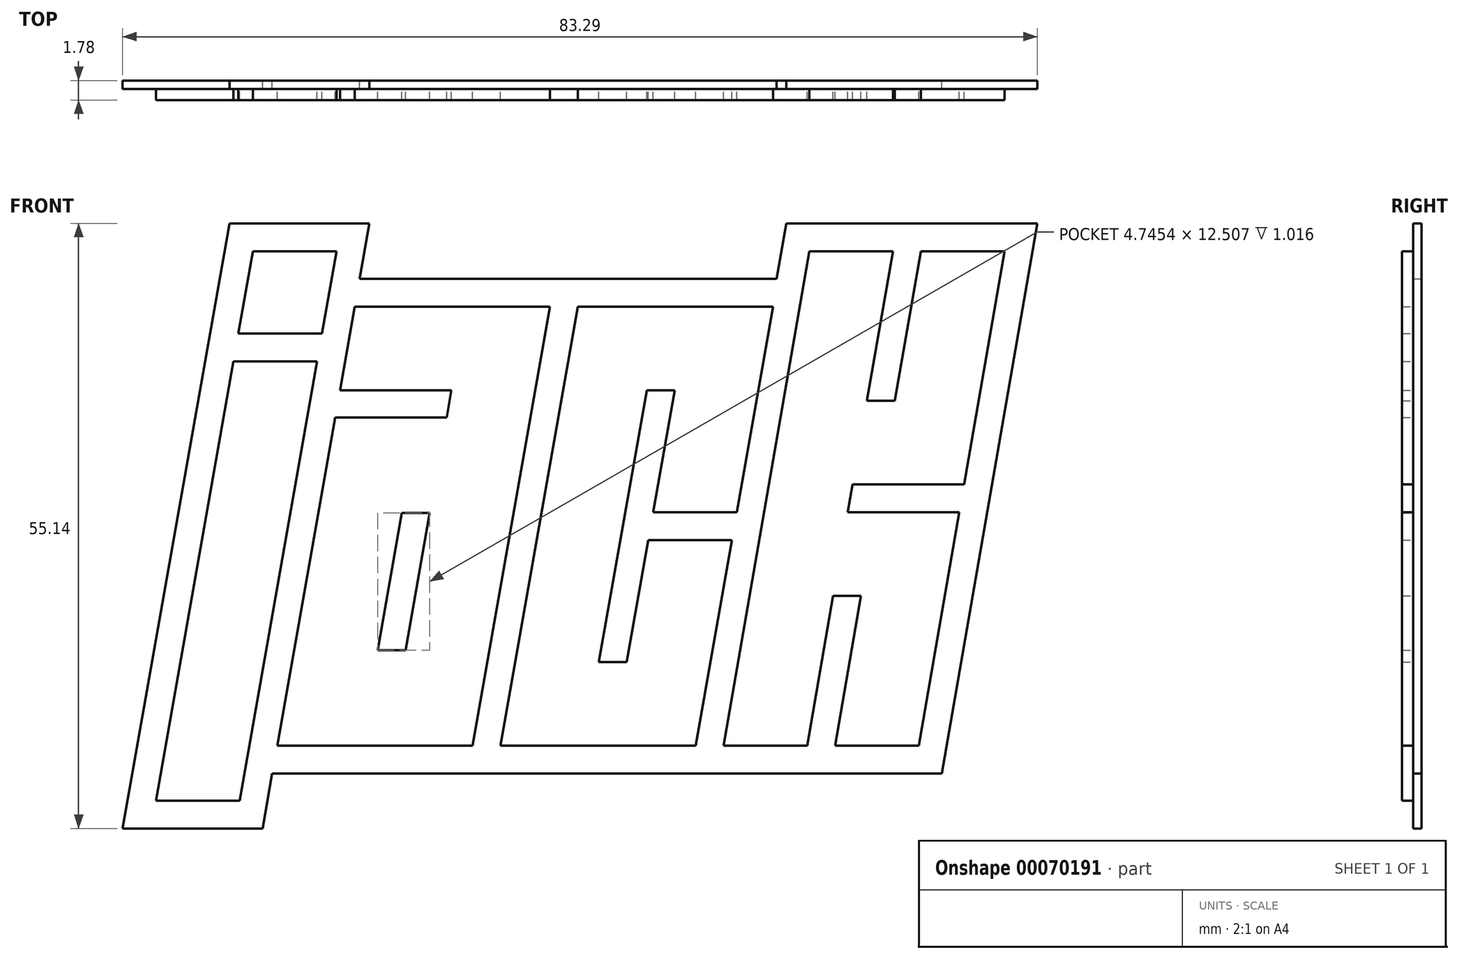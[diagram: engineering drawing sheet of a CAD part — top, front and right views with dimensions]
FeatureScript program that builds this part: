
annotation { "Feature Type Name" : "Feature", "Feature Type Description" : "" }
export const myFeature = defineFeature(function(context is Context, id is Id, definition is map)
    precondition{}
    {
        {
            var Q0;
            Q0=qCreatedBy(makeId("Front.planeOp"),FACE);
            var sketch = newSketch(context, id + "F0", { "sketchPlane" : qUnion([Q0])});
            skLineSegment(sketch, "E0", {"start": v(0, 0) * mm, "end": v(6.17, 35.02) * mm});
            skLineSegment(sketch, "E1", {"start": v(6.17, 35.02) * mm, "end": v(13.8, 35.02) * mm});
            skLineSegment(sketch, "E2", {"start": v(13.8, 35.02) * mm, "end": v(7.62, 0) * mm});
            skLineSegment(sketch, "E3", {"start": v(0, 0) * mm, "end": v(7.62, 0) * mm});
            skLineSegment(sketch, "E4", {"start": v(6.62, 37.56) * mm, "end": v(14.24, 37.56) * mm});
            skLineSegment(sketch, "E5", {"start": v(14.24, 37.56) * mm, "end": v(15.57, 45.06) * mm});
            skLineSegment(sketch, "E6", {"start": v(15.57, 45.06) * mm, "end": v(7.95, 45.06) * mm});
            skLineSegment(sketch, "E7", {"start": v(7.95, 45.06) * mm, "end": v(6.62, 37.56) * mm});
            skLineSegment(sketch, "E8", {"start": v(0, 0) * mm, "end": v(-0.88, -5) * mm});
            skLineSegment(sketch, "E9", {"start": v(-0.88, -5) * mm, "end": v(6.74, -5) * mm});
            skLineSegment(sketch, "E10", {"start": v(6.74, -5) * mm, "end": v(7.62, 0) * mm});
            skLineSegment(sketch, "E11.0", {"start": v(-3.9, -7.54) * mm, "end": v(8.83, -7.54) * mm});
            skLineSegment(sketch, "E11.1", {"start": v(-2.5, 0.44) * mm, "end": v(-3.9, -7.54) * mm});
            skLineSegment(sketch, "E11.2", {"start": v(18.55, 47.6) * mm, "end": v(5.81, 47.6) * mm});
            skLineSegment(sketch, "E11.5", {"start": v(-2.5, 0.44) * mm, "end": v(5.81, 47.6) * mm});
            skLineSegment(sketch, "E12", {"start": v(10.16, 0) * mm, "end": v(27.94, 0) * mm});
            skLineSegment(sketch, "E13", {"start": v(27.94, 0) * mm, "end": v(35, 40.02) * mm});
            skLineSegment(sketch, "E14", {"start": v(35, 40.02) * mm, "end": v(17.22, 40.02) * mm});
            skLineSegment(sketch, "E15", {"start": v(17.22, 40.02) * mm, "end": v(15.87, 32.4) * mm});
            skLineSegment(sketch, "E16", {"start": v(15.87, 32.4) * mm, "end": v(26.03, 32.4) * mm});
            skLineSegment(sketch, "E17", {"start": v(26.03, 32.4) * mm, "end": v(25.6, 29.9) * mm});
            skLineSegment(sketch, "E18", {"start": v(25.6, 29.9) * mm, "end": v(15.43, 29.9) * mm});
            skLineSegment(sketch, "E19", {"start": v(21.52, 21.2) * mm, "end": v(19.31, 8.7) * mm});
            skLineSegment(sketch, "E20", {"start": v(19.31, 8.7) * mm, "end": v(21.85, 8.7) * mm});
            skLineSegment(sketch, "E21", {"start": v(21.85, 8.7) * mm, "end": v(24.06, 21.2) * mm});
            skLineSegment(sketch, "E22", {"start": v(24.06, 21.2) * mm, "end": v(21.52, 21.2) * mm});
            skLineSegment(sketch, "E23", {"start": v(15.43, 29.9) * mm, "end": v(12.9, 29.9) * mm});
            skLineSegment(sketch, "E24", {"start": v(15.57, 45.06) * mm, "end": v(15.57, 47.6) * mm, "construction": true});
            skLineSegment(sketch, "E25", {"start": v(6.62, 37.56) * mm, "end": v(6.62, 35.02) * mm, "construction": true});
            skLineSegment(sketch, "E26", {"start": v(10.16, 0) * mm, "end": v(15.43, 29.9) * mm});
            skLineSegment(sketch, "E27", {"start": v(19.31, 8.7) * mm, "end": v(11.7, 8.7) * mm, "construction": true});
            skLineSegment(sketch, "E28", {"start": v(21.85, 8.7) * mm, "end": v(29.47, 8.7) * mm, "construction": true});
            skLineSegment(sketch, "E29", {"start": v(8.83, -7.54) * mm, "end": v(9.71, -2.54) * mm});
            skLineSegment(sketch, "E30", {"start": v(9.71, -2.54) * mm, "end": v(70.68, -2.54) * mm});
            skLineSegment(sketch, "E31", {"start": v(24.06, 21.2) * mm, "end": v(24.06, 29.9) * mm, "construction": true});
            skLineSegment(sketch, "E32", {"start": v(21.85, 8.7) * mm, "end": v(21.85, 0) * mm, "construction": true});
            skLineSegment(sketch, "E33", {"start": v(30.48, 0) * mm, "end": v(37.54, 40.02) * mm});
            skLineSegment(sketch, "E34", {"start": v(37.54, 40.02) * mm, "end": v(55.32, 40.02) * mm});
            skLineSegment(sketch, "E35", {"start": v(55.32, 40.02) * mm, "end": v(52.01, 21.28) * mm});
            skLineSegment(sketch, "E36", {"start": v(52.01, 21.28) * mm, "end": v(44.4, 21.28) * mm});
            skLineSegment(sketch, "E37", {"start": v(44.4, 21.28) * mm, "end": v(46.35, 32.4) * mm});
            skLineSegment(sketch, "E38", {"start": v(46.35, 32.4) * mm, "end": v(43.81, 32.4) * mm});
            skLineSegment(sketch, "E39", {"start": v(43.81, 32.4) * mm, "end": v(39.44, 7.62) * mm});
            skLineSegment(sketch, "E40", {"start": v(39.44, 7.62) * mm, "end": v(41.98, 7.62) * mm});
            skLineSegment(sketch, "E41", {"start": v(41.98, 7.62) * mm, "end": v(43.94, 18.74) * mm});
            skLineSegment(sketch, "E42", {"start": v(43.94, 18.74) * mm, "end": v(51.56, 18.74) * mm});
            skLineSegment(sketch, "E43", {"start": v(51.56, 18.74) * mm, "end": v(48.26, 0) * mm});
            skLineSegment(sketch, "E44", {"start": v(48.26, 0) * mm, "end": v(30.48, 0) * mm});
            skLineSegment(sketch, "E45", {"start": v(31.06, 17.72) * mm, "end": v(33.6, 17.72) * mm, "construction": true});
            skLineSegment(sketch, "E46", {"start": v(27.94, 0) * mm, "end": v(27.94, -2.54) * mm, "construction": true});
            skLineSegment(sketch, "E47", {"start": v(44.4, 21.28) * mm, "end": v(44.4, 18.74) * mm, "construction": true});
            skLineSegment(sketch, "E48", {"start": v(44.4, 21.28) * mm, "end": v(41.85, 21.28) * mm, "construction": true});
            skLineSegment(sketch, "E49", {"start": v(43.81, 32.4) * mm, "end": v(43.81, 40.02) * mm, "construction": true});
            skLineSegment(sketch, "E50", {"start": v(39.44, 7.62) * mm, "end": v(39.44, 0) * mm, "construction": true});
            skLineSegment(sketch, "E51", {"start": v(39.44, 7.62) * mm, "end": v(31.82, 7.62) * mm, "construction": true});
            skLineSegment(sketch, "E52", {"start": v(46.35, 32.4) * mm, "end": v(53.97, 32.4) * mm, "construction": true});
            skLineSegment(sketch, "E53", {"start": v(41.98, 7.62) * mm, "end": v(49.6, 7.62) * mm, "construction": true});
            skLineSegment(sketch, "E54", {"start": v(58.62, 45.06) * mm, "end": v(50.8, 0) * mm});
            skLineSegment(sketch, "E55", {"start": v(50.8, 0) * mm, "end": v(58.42, 0) * mm});
            skLineSegment(sketch, "E56", {"start": v(58.42, 0) * mm, "end": v(60.79, 13.64) * mm});
            skLineSegment(sketch, "E57", {"start": v(60.79, 13.64) * mm, "end": v(63.33, 13.64) * mm});
            skLineSegment(sketch, "E58", {"start": v(63.33, 13.64) * mm, "end": v(60.96, 0) * mm});
            skLineSegment(sketch, "E59", {"start": v(60.96, 0) * mm, "end": v(68.58, 0) * mm});
            skLineSegment(sketch, "E60", {"start": v(68.58, 0) * mm, "end": v(72.27, 21.26) * mm});
            skLineSegment(sketch, "E61", {"start": v(72.27, 21.26) * mm, "end": v(62.1, 21.26) * mm});
            skLineSegment(sketch, "E62", {"start": v(62.1, 21.26) * mm, "end": v(62.55, 23.8) * mm});
            skLineSegment(sketch, "E63", {"start": v(62.55, 23.8) * mm, "end": v(72.7, 23.8) * mm});
            skLineSegment(sketch, "E64", {"start": v(72.7, 23.8) * mm, "end": v(76.4, 45.06) * mm});
            skLineSegment(sketch, "E65", {"start": v(76.4, 45.06) * mm, "end": v(68.78, 45.06) * mm});
            skLineSegment(sketch, "E66", {"start": v(68.78, 45.06) * mm, "end": v(66.41, 31.42) * mm});
            skLineSegment(sketch, "E67", {"start": v(66.41, 31.42) * mm, "end": v(63.87, 31.42) * mm});
            skLineSegment(sketch, "E68", {"start": v(63.87, 31.42) * mm, "end": v(66.24, 45.06) * mm});
            skLineSegment(sketch, "E69", {"start": v(66.24, 45.06) * mm, "end": v(58.62, 45.06) * mm});
            skLineSegment(sketch, "E70", {"start": v(48.26, 0) * mm, "end": v(50.8, 0) * mm, "construction": true});
            skLineSegment(sketch, "E71", {"start": v(56.25, 31.42) * mm, "end": v(63.87, 31.42) * mm, "construction": true});
            skLineSegment(sketch, "E72", {"start": v(63.87, 31.42) * mm, "end": v(63.87, 23.8) * mm, "construction": true});
            skLineSegment(sketch, "E73", {"start": v(63.33, 13.64) * mm, "end": v(63.33, 21.26) * mm, "construction": true});
            skLineSegment(sketch, "E74", {"start": v(66.41, 31.42) * mm, "end": v(74.03, 31.42) * mm, "construction": true});
            skLineSegment(sketch, "E75", {"start": v(63.33, 13.64) * mm, "end": v(70.95, 13.64) * mm, "construction": true});
            skLineSegment(sketch, "E76", {"start": v(60.79, 13.64) * mm, "end": v(53.17, 13.64) * mm, "construction": true});
            skLineSegment(sketch, "E77", {"start": v(72.27, 21.26) * mm, "end": v(72.27, 23.8) * mm, "construction": true});
            skLineSegment(sketch, "E78", {"start": v(57.98, -2.54) * mm, "end": v(60.52, -2.54) * mm, "construction": true});
            skLineSegment(sketch, "E79", {"start": v(68.78, 45.06) * mm, "end": v(68.78, 23.8) * mm, "construction": true});
            skLineSegment(sketch, "E80", {"start": v(68.58, 0) * mm, "end": v(68.58, 21.26) * mm, "construction": true});
            skLineSegment(sketch, "E81", {"start": v(18.55, 47.6) * mm, "end": v(17.66, 42.56) * mm});
            skLineSegment(sketch, "E82", {"start": v(17.66, 42.56) * mm, "end": v(55.64, 42.56) * mm});
            skLineSegment(sketch, "E83", {"start": v(55.64, 42.56) * mm, "end": v(56.52, 47.6) * mm});
            skLineSegment(sketch, "E84", {"start": v(79.38, 47.6) * mm, "end": v(70.68, -2.54) * mm});
            skLineSegment(sketch, "E85", {"start": v(56.52, 47.6) * mm, "end": v(79.38, 47.6) * mm});
            skLineSegment(sketch, "E86", {"start": v(55.64, 42.56) * mm, "end": v(58.18, 42.56) * mm, "construction": true});
            skLineSegment(sketch, "E87", {"start": v(68.58, 0) * mm, "end": v(71.12, 0) * mm, "construction": true});
            skLineSegment(sketch, "E88", {"start": v(68.58, 0) * mm, "end": v(68.58, -2.54) * mm, "construction": true});
            skSolve(sketch);
        }
        {
            var Q0;
            Q0=makeQuery(id+"F0.imprint","IMPRINT",FACE,{"disambiguationData":[TD([[makeQuery(id+"F0.imprint","IMPRINT",EDGE,{"derivedFrom":sQuery(id+"F0.wireOp",EDGE,"E0")}),1.0]])]});
            var Q1;
            Q1=makeQuery(id+"F0.imprint","IMPRINT",FACE,{"disambiguationData":[TD([[makeQuery(id+"F0.imprint","IMPRINT",EDGE,{"derivedFrom":sQuery(id+"F0.wireOp",EDGE,"E19")}),1.0]])]});
            extrude(context, id + "F1", {"entities" : qUnion([Q0, Q1]), "offsetDistance" : 25.4 * mm, "depth" : 0.76 * mm});
        }
        {
            var Q0;
            Q0=makeQuery(id+"F0.imprint","IMPRINT",FACE,{"disambiguationData":[TD([[makeQuery(id+"F0.imprint","IMPRINT",EDGE,{"derivedFrom":sQuery(id+"F0.wireOp",EDGE,"E0")}),-1.0]])]});
            var Q1;
            Q1=makeQuery(id+"F0.imprint","IMPRINT",FACE,{"disambiguationData":[TD([[makeQuery(id+"F0.imprint","IMPRINT",EDGE,{"derivedFrom":sQuery(id+"F0.wireOp",EDGE,"E3")}),-1.0]])]});
            var Q2;
            Q2=makeQuery(id+"F0.imprint","IMPRINT",FACE,{"disambiguationData":[TD([[makeQuery(id+"F0.imprint","IMPRINT",EDGE,{"derivedFrom":sQuery(id+"F0.wireOp",EDGE,"E4")}),1.0]])]});
            var Q3;
            Q3=makeQuery(id+"F0.imprint","IMPRINT",FACE,{"disambiguationData":[TD([[makeQuery(id+"F0.imprint","IMPRINT",EDGE,{"derivedFrom":sQuery(id+"F0.wireOp",EDGE,"E12")}),1.0]])]});
            var Q4;
            Q4=makeQuery(id+"F0.imprint","IMPRINT",FACE,{"disambiguationData":[TD([[makeQuery(id+"F0.imprint","IMPRINT",EDGE,{"derivedFrom":sQuery(id+"F0.wireOp",EDGE,"E33")}),-1.0]])]});
            var Q5;
            Q5=makeQuery(id+"F0.imprint","IMPRINT",FACE,{"disambiguationData":[TD([[makeQuery(id+"F0.imprint","IMPRINT",EDGE,{"derivedFrom":sQuery(id+"F0.wireOp",EDGE,"E54")}),1.0]])]});
            extrude(context, id + "F2", {"entities" : qUnion([Q0, Q1, Q2, Q3, Q4, Q5]), "operationType" : NewBodyOperationType.ADD, "offsetDistance" : 25.4 * mm, "depth" : 1.78 * mm});
        }
    });
